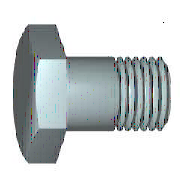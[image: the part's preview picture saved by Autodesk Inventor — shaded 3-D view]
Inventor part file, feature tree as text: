
AUTODESK INVENTOR PART (.ipt)
format: ipt  version: 2020 (Build 240168000, 168)  size: 191,488 bytes
history: native  units: mm (DEFAULTED — no unit token found)
features: sketch x3, other x1, extrude x1, chamfer x1, plane x1
ambient origin geometry x7: Origin, YZ Plane, XZ Plane, X Axis, Y Axis, Z Axis, Center Point
bodies: Solid1 (feature_tree)
feature tree (7):
  other  "轴承体"
  extrude  "头"  Depth=26.0mm
  chamfer  "倒角1"  Distance=6.0mm
  plane  "Work Plane1"
  sketch  "草图1"  dims[d0=35.0mm d1=26.0mm]
  sketch  "草图2"  dims[d2=10.0mm]
  sketch  "草图4"  dims[d12=90.0deg d3=6.0mm d4=0.0mm d5=30.0deg d21=90.0deg d6=0.920175mm d7=0.920275mm d8=0.0mm d9=0.4001mm d10=14.5mm d11=16.0mm d13=0.920275mm d14=10.0mm d15=26.0mm d16=0.0mm d19=16.0mm d55=45.0deg d57=0.0mm d58=0.0mm]
